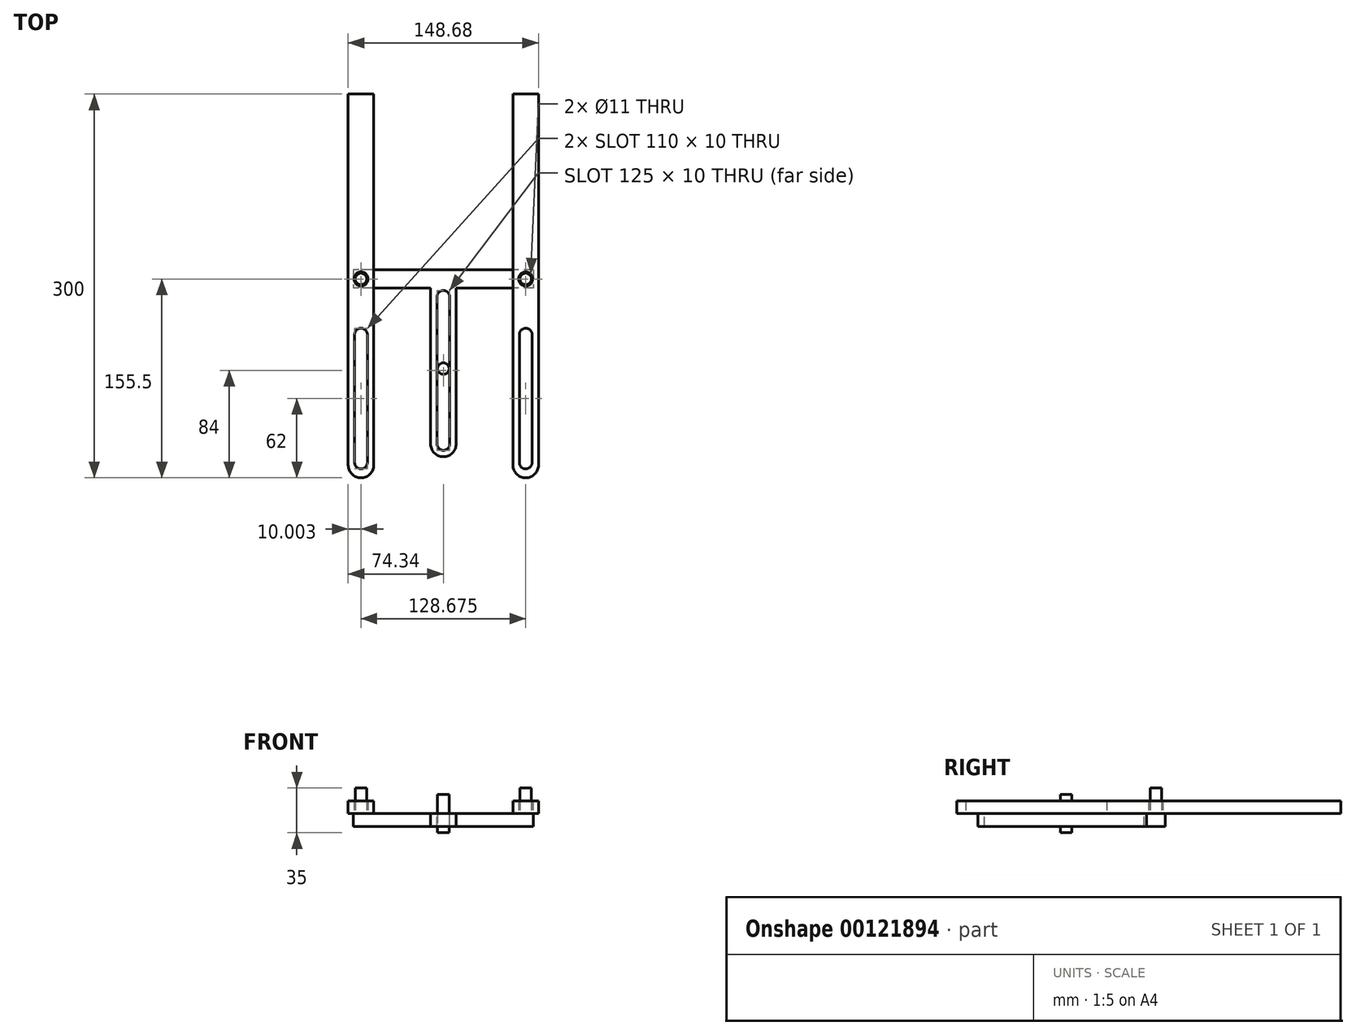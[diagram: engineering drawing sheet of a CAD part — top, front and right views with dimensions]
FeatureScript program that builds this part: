
annotation { "Feature Type Name" : "Feature", "Feature Type Description" : "" }
export const myFeature = defineFeature(function(context is Context, id is Id, definition is map)
    precondition{}
    {
        {
            var Q0;
            Q0=qCreatedBy(makeId("Top.planeOp"),FACE);
            var sketch = newSketch(context, id + "F0", { "sketchPlane" : qUnion([Q0])});
            skLineSegment(sketch, "E0.bottom", {"start": v(70.34, 7.21) * mm, "end": v(-70.34, 7.21) * mm});
            skLineSegment(sketch, "E0.top", {"start": v(70.34, -7.21) * mm, "end": v(-70.34, -7.21) * mm});
            skLineSegment(sketch, "E0.left", {"start": v(70.34, 7.21) * mm, "end": v(70.34, -7.21) * mm});
            skLineSegment(sketch, "E0.right", {"start": v(-70.34, 7.21) * mm, "end": v(-70.34, -7.21) * mm});
            skPoint(sketch, "E0.middle", {"position": v(0, 0) * mm});
            skSolve(sketch);
        }
        {
            var Q0;
            Q0=makeQuery(id+"F0.imprint","IMPRINT",FACE,{"disambiguationData":[TD([[makeQuery(id+"F0.imprint","IMPRINT",EDGE,{"derivedFrom":sQuery(id+"F0.wireOp",EDGE,"E0.bottom")}),1.0]])]});
            extrude(context, id + "F1", {"entities" : qUnion([Q0]), "oppositeDirection" : true, "depth" : 10 * mm});
        }
        {
            var Q0;
            Q0=makeQuery(id+"F1.opExtrude","CAP_FACE",FACE,{"disambiguationData":[OSD([sQuery(id+"F0.wireOp",EDGE,"E0.bottom"),sQuery(id+"F0.wireOp",EDGE,"E0.top"),sQuery(id+"F0.wireOp",EDGE,"E0.left"),sQuery(id+"F0.wireOp",EDGE,"E0.right")])],"isStart":true});
            var sketch = newSketch(context, id + "F2", { "sketchPlane" : qUnion([Q0])});
            skCircle(sketch, "E1", {"center": v(-64.34, 0) * mm, "radius": 4.5 * mm});
            skCircle(sketch, "E2", {"center": v(64.34, 0) * mm, "radius": 4.5 * mm});
            skLineSegment(sketch, "E3", {"start": v(-64.34, 0) * mm, "end": v(64.34, 0) * mm, "construction": true});
            skSolve(sketch);
        }
        {
            var Q0;
            Q0 = qSketchRegion(id + "F2", true);
            extrude(context, id + "F3", {"entities" : qUnion([Q0]), "operationType" : NewBodyOperationType.ADD, "depth" : 20 * mm});
        }
        {
            var Q0;
            Q0=makeQuery(id+"F1.opExtrude","CAP_FACE",FACE,{"disambiguationData":[OSD([sQuery(id+"F0.wireOp",EDGE,"E0.bottom"),sQuery(id+"F0.wireOp",EDGE,"E0.top"),sQuery(id+"F0.wireOp",EDGE,"E0.left"),sQuery(id+"F0.wireOp",EDGE,"E0.right")])],"isStart":true});
            var sketch = newSketch(context, id + "F4", { "sketchPlane" : qUnion([Q0])});
            skLineSegment(sketch, "E4", {"start": v(-64.34, 144.5) * mm, "end": v(-64.34, -144.5) * mm, "construction": true});
            skPoint(sketch, "E5", {"position": v(-64.34, 0) * mm});
            skLineSegment(sketch, "E6.bottom", {"start": v(-74.34, 144.5) * mm, "end": v(-54.34, 144.5) * mm});
            skLineSegment(sketch, "E6.top", {"start": v(-74.34, -155.5) * mm, "end": v(-54.34, -155.5) * mm});
            skLineSegment(sketch, "E6.left", {"start": v(-74.34, 144.5) * mm, "end": v(-74.34, -155.5) * mm});
            skLineSegment(sketch, "E6.right", {"start": v(-54.34, 144.5) * mm, "end": v(-54.34, -155.5) * mm});
            skCircle(sketch, "E7", {"center": v(-64.34, 0) * mm, "radius": 5.5 * mm});
            skArc(sketch, "E8", {"start": v(-59.34, -43.5) * mm, "mid": v(-64.34, -38.5) * mm, "end": v(-69.34, -43.5) * mm});
            skArc(sketch, "E9", {"start": v(-69.34, -143.5) * mm, "mid": v(-64.34, -148.5) * mm, "end": v(-59.34, -143.5) * mm});
            skLineSegment(sketch, "E10", {"start": v(-69.34, -43.5) * mm, "end": v(-69.34, -143.5) * mm});
            skLineSegment(sketch, "E11", {"start": v(-59.34, -143.5) * mm, "end": v(-59.34, -43.5) * mm});
            skSolve(sketch);
        }
        {
            var Q0;
            {var subQ5=sQuery(id+"F4.wireOp",EDGE,"E6.bottom");Q0=makeQuery(id+"F4.imprint","IMPRINT",FACE,{"disambiguationData":[TD([[makeQuery(id+"F4.imprint","IMPRINT",EDGE,{"derivedFrom":subQ5}),-1.0]])]});}
            var Q1;
            Q1=makeQuery(id+"F4.imprint","IMPRINT",FACE,{"disambiguationData":[TD([[makeQuery(id+"F4.imprint","IMPRINT",EDGE,{"derivedFrom":sQuery(id+"F4.wireOp",EDGE,"E7")}),-1.0]])]});
            extrude(context, id + "F5", {"entities" : qUnion([Q0, Q1]), "depth" : 10 * mm});
        }
        {
            var Q0;
            Q0=makeQuery(id+"F5.opExtrude","SWEPT_BODY",BODY,{"disambiguationData":[OSD([sQuery(id+"F4.wireOp",EDGE,"E6.bottom"),sQuery(id+"F4.wireOp",EDGE,"E6.top"),sQuery(id+"F4.wireOp",EDGE,"E6.left"),sQuery(id+"F4.wireOp",EDGE,"E6.right"),sQuery(id+"F4.wireOp",EDGE,"E7"),sQuery(id+"F4.wireOp",EDGE,"E8"),sQuery(id+"F4.wireOp",EDGE,"E9"),sQuery(id+"F4.wireOp",EDGE,"E10"),sQuery(id+"F4.wireOp",EDGE,"E11")])]});
            var Q1;
            Q1=qCreatedBy(makeId("Right.planeOp"),FACE);
            mirror(context, id + "F6", {"entities" : qUnion([Q0]), "mirrorPlane" : qUnion([Q1])});
        }
        {
            var Q0;
            Q0=qCreatedBy(makeId("Top.planeOp"),FACE);
            var sketch = newSketch(context, id + "F7", { "sketchPlane" : qUnion([Q0])});
            skCircle(sketch, "E12", {"center": v(0, -70.08) * mm, "radius": 4.5 * mm});
            skSolve(sketch);
        }
        {
            var Q0;
            Q0 = qSketchRegion(id + "F7", true);
            extrude(context, id + "F8", {"entities" : qUnion([Q0]), "endBound" : BoundingType.SYMMETRIC, "depth" : 30 * mm});
        }
        {
            var Q0;
            Q0=makeQuery(id+"F1.opExtrude","CAP_FACE",FACE,{"disambiguationData":[OSD([sQuery(id+"F0.wireOp",EDGE,"E0.bottom"),sQuery(id+"F0.wireOp",EDGE,"E0.top"),sQuery(id+"F0.wireOp",EDGE,"E0.left"),sQuery(id+"F0.wireOp",EDGE,"E0.right")])],"isStart":true});
            var sketch = newSketch(context, id + "F9", { "sketchPlane" : qUnion([Q0])});
            skLineSegment(sketch, "E13.bottom", {"start": v(-10, 0) * mm, "end": v(10, 0) * mm});
            skLineSegment(sketch, "E13.top", {"start": v(-10, -139) * mm, "end": v(10, -139) * mm});
            skLineSegment(sketch, "E13.left", {"start": v(-10, 0) * mm, "end": v(-10, -139) * mm});
            skLineSegment(sketch, "E13.right", {"start": v(10, 0) * mm, "end": v(10, -139) * mm});
            skCircle(sketch, "E14", {"center": v(0, -14) * mm, "radius": 5 * mm});
            skCircle(sketch, "E15", {"center": v(0, -129) * mm, "radius": 5 * mm});
            skLineSegment(sketch, "E16", {"start": v(-5, -14) * mm, "end": v(-5, -129) * mm});
            skLineSegment(sketch, "E17", {"start": v(5, -129) * mm, "end": v(5, -14) * mm});
            skSolve(sketch);
        }
        {
            var Q0;
            {var subQ4=sQuery(id+"F9.wireOp",EDGE,"E13.top");Q0=makeQuery(id+"F9.imprint","IMPRINT",FACE,{"disambiguationData":[TD([[makeQuery(id+"F9.imprint","IMPRINT",EDGE,{"derivedFrom":subQ4}),1.0]])]});}
            var Q1;
            Q1=makeQuery(id+"F1.opExtrude","CAP_FACE",FACE,{"disambiguationData":[OSD([sQuery(id+"F0.wireOp",EDGE,"E0.bottom"),sQuery(id+"F0.wireOp",EDGE,"E0.top"),sQuery(id+"F0.wireOp",EDGE,"E0.left"),sQuery(id+"F0.wireOp",EDGE,"E0.right")])],"isStart":false});
            extrude(context, id + "F10", {"entities" : qUnion([Q0]), "operationType" : NewBodyOperationType.ADD, "endBound" : BoundingType.UP_TO_SURFACE, "oppositeDirection" : true, "endBoundEntityFace" : qUnion([Q1]), "depth" : 25 * mm});
        }
        {
            var Q0;
            Q0=makeQuery(id+"F5.opExtrude","SWEPT_EDGE",EDGE,{"disambiguationData":[OSD([sQuery(id+"F4.wireOp",EDGE,"E6.top"),sQuery(id+"F4.wireOp",EDGE,"E6.left")])]});
            var Q1;
            Q1=makeQuery(id+"F5.opExtrude","SWEPT_EDGE",EDGE,{"disambiguationData":[OSD([sQuery(id+"F4.wireOp",EDGE,"E6.top"),sQuery(id+"F4.wireOp",EDGE,"E6.right")])]});
            fillet(context, id + "F11", {"entities" : qUnion([Q0, Q1]), "radius" : 10 * mm, "tangentPropagation" : true, "allowEdgeOverflow" : false});
        }
        {
            var Q0;
            Q0=makeQuery(id+"F6.opPattern","COPY",EDGE,{"derivedFrom":makeQuery(id+"F5.opExtrude","SWEPT_EDGE",EDGE,{"disambiguationData":[OSD([sQuery(id+"F4.wireOp",EDGE,"E6.top"),sQuery(id+"F4.wireOp",EDGE,"E6.right")])]}),"instanceName":"1"});
            var Q1;
            Q1=makeQuery(id+"F6.opPattern","COPY",EDGE,{"derivedFrom":makeQuery(id+"F5.opExtrude","SWEPT_EDGE",EDGE,{"disambiguationData":[OSD([sQuery(id+"F4.wireOp",EDGE,"E6.top"),sQuery(id+"F4.wireOp",EDGE,"E6.left")])]}),"instanceName":"1"});
            fillet(context, id + "F12", {"entities" : qUnion([Q0, Q1]), "radius" : 10 * mm, "tangentPropagation" : true, "allowEdgeOverflow" : false});
        }
        {
            var Q0;
            Q0=makeQuery(id+"F10.opExtrude","SWEPT_EDGE",EDGE,{"disambiguationData":[OSD([sQuery(id+"F9.wireOp",EDGE,"E13.top"),sQuery(id+"F9.wireOp",EDGE,"E13.left")])]});
            var Q1;
            Q1=makeQuery(id+"F10.opExtrude","SWEPT_EDGE",EDGE,{"disambiguationData":[OSD([sQuery(id+"F9.wireOp",EDGE,"E13.top"),sQuery(id+"F9.wireOp",EDGE,"E13.right")])]});
            fillet(context, id + "F13", {"entities" : qUnion([Q0, Q1]), "radius" : 10 * mm, "tangentPropagation" : true, "allowEdgeOverflow" : false});
        }
    });
